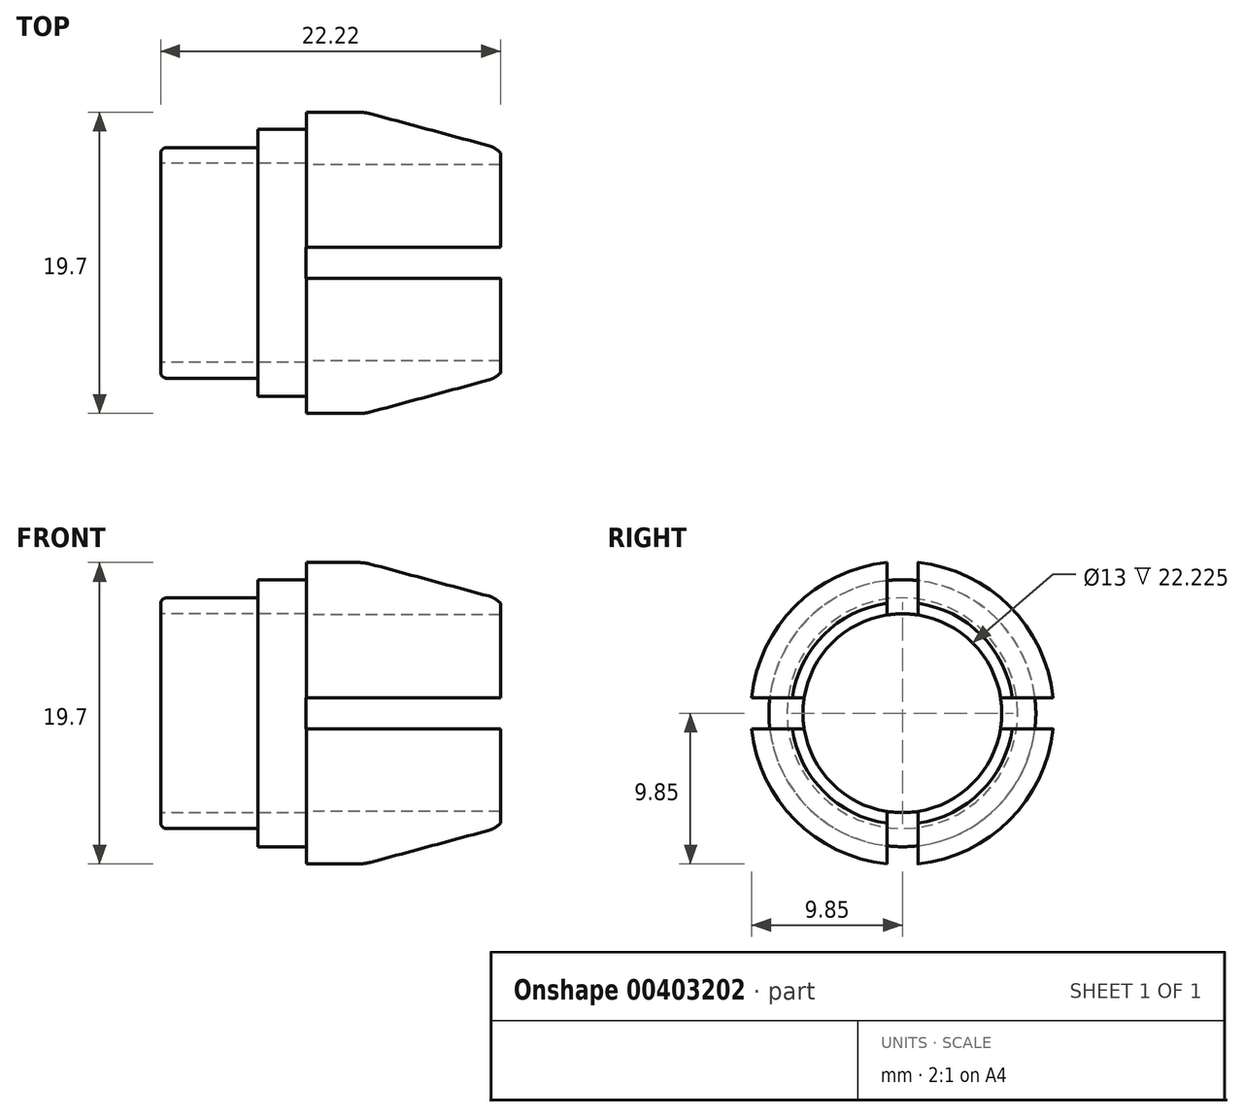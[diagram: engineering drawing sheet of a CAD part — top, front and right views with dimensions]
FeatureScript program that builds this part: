
annotation { "Feature Type Name" : "Feature", "Feature Type Description" : "" }
export const myFeature = defineFeature(function(context is Context, id is Id, definition is map)
    precondition{}
    {
        {
            var Q0;
            Q0=qCreatedBy(makeId("Front.planeOp"),FACE);
            var sketch = newSketch(context, id + "F0", { "sketchPlane" : qUnion([Q0])});
            skLineSegment(sketch, "E0", {"start": v(-22.22, 0) * mm, "end": v(21.75, 0) * mm, "construction": true});
            skLineSegment(sketch, "E1", {"start": v(7.6, 7.73) * mm, "end": v(-0.11, 9.8) * mm});
            skLineSegment(sketch, "E2", {"start": v(-0.93, 9.9) * mm, "end": v(-4.33, 9.9) * mm});
            skArc(sketch, "E3.filletArc", {"start": v(8.37, 7.26) * mm, "mid": v(8.02, 7.55) * mm, "end": v(7.6, 7.73) * mm});
            skLineSegment(sketch, "E4", {"start": v(-4.33, 9.9) * mm, "end": v(-4.33, 8.73) * mm});
            skLineSegment(sketch, "E5", {"start": v(-4.33, 8.73) * mm, "end": v(-7.5, 8.73) * mm});
            skLineSegment(sketch, "E6", {"start": v(-7.5, 8.73) * mm, "end": v(-7.5, 7.54) * mm});
            skLineSegment(sketch, "E7", {"start": v(-7.5, 7.54) * mm, "end": v(-13.45, 7.54) * mm});
            skLineSegment(sketch, "E8", {"start": v(-13.85, 6.5) * mm, "end": v(8.37, 6.5) * mm});
            skLineSegment(sketch, "E9", {"start": v(8.37, 7.26) * mm, "end": v(8.37, 6.5) * mm});
            skLineSegment(sketch, "E10", {"start": v(-13.85, 7.15) * mm, "end": v(-13.85, 6.5) * mm});
            skPoint(sketch, "E11.visualSharp", {"position": v(-13.85, 7.54) * mm});
            skArc(sketch, "E11.filletArc", {"start": v(-13.45, 7.54) * mm, "mid": v(-13.74, 7.43) * mm, "end": v(-13.85, 7.15) * mm});
            skPoint(sketch, "E12.visualSharp", {"position": v(-0.52, 9.9) * mm});
            skArc(sketch, "E12.filletArc", {"start": v(-0.11, 9.8) * mm, "mid": v(-0.52, 9.88) * mm, "end": v(-0.93, 9.9) * mm});
            skSolve(sketch);
        }
        {
            var Q0;
            Q0=makeQuery(id+"F0.imprint","IMPRINT",FACE,{"disambiguationData":[TD([[makeQuery(id+"F0.imprint","IMPRINT",EDGE,{"derivedFrom":sQuery(id+"F0.wireOp",EDGE,"E1")}),1.0]])]});
            var Q1;
            Q1=qSketchRegion(id+"F2",true);
            var Q2;
            Q2=sQuery(id+"F0.wireOp",EDGE,"E0");
            revolve(context, id + "F1", {"entities" : qUnion([Q0, Q1]), "axis" : qUnion([Q2]), "revolveType" : RevolveType.FULL});
        }
        {
            var Q0;
            Q0=qCreatedBy(makeId("Right.planeOp"),FACE);
            var sketch = newSketch(context, id + "F2", { "sketchPlane" : qUnion([Q0])});
            skCircle(sketch, "E13", {"center": v(0, 0) * mm, "radius": 8.53 * mm, "construction": true});
            skPoint(sketch, "E14", {"position": v(0, -8.53) * mm});
            skPoint(sketch, "E15", {"position": v(8.53, 0) * mm});
            skLineSegment(sketch, "E16", {"start": v(1.02, -9.93) * mm, "end": v(-1.02, -9.93) * mm});
            skLineSegment(sketch, "E17", {"start": v(-1.02, -9.93) * mm, "end": v(-1.02, -6.38) * mm});
            skLineSegment(sketch, "E18", {"start": v(-1.02, -6.38) * mm, "end": v(1.02, -6.38) * mm});
            skLineSegment(sketch, "E19", {"start": v(1.02, -6.38) * mm, "end": v(1.02, -9.93) * mm});
            skPoint(sketch, "E20", {"position": v(0, 8.53) * mm});
            skLineSegment(sketch, "E21", {"start": v(1.02, 6.38) * mm, "end": v(-1.02, 6.38) * mm});
            skLineSegment(sketch, "E22", {"start": v(-1.02, 6.38) * mm, "end": v(-1.02, 9.93) * mm});
            skLineSegment(sketch, "E23", {"start": v(-1.02, 9.93) * mm, "end": v(1.02, 9.93) * mm});
            skLineSegment(sketch, "E24", {"start": v(1.02, 9.93) * mm, "end": v(1.02, 6.38) * mm});
            skLineSegment(sketch, "E25", {"start": v(-9.93, -1.02) * mm, "end": v(-9.93, 1.02) * mm});
            skLineSegment(sketch, "E26", {"start": v(-9.93, 1.02) * mm, "end": v(-6.38, 1.02) * mm});
            skLineSegment(sketch, "E27", {"start": v(-6.38, 1.02) * mm, "end": v(-6.38, -1.02) * mm});
            skLineSegment(sketch, "E28", {"start": v(-6.38, -1.02) * mm, "end": v(-9.93, -1.02) * mm});
            skLineSegment(sketch, "E29", {"start": v(-10.98, 0) * mm, "end": v(11.1, 0) * mm, "construction": true});
            skLineSegment(sketch, "E30", {"start": v(6.38, -1.02) * mm, "end": v(6.38, 1.02) * mm});
            skLineSegment(sketch, "E31", {"start": v(6.38, 1.02) * mm, "end": v(9.93, 1.02) * mm});
            skLineSegment(sketch, "E32", {"start": v(9.93, 1.02) * mm, "end": v(9.93, -1.02) * mm});
            skLineSegment(sketch, "E33", {"start": v(9.93, -1.02) * mm, "end": v(6.38, -1.02) * mm});
            skSolve(sketch);
        }
        {
            var Q0;
            Q0=qSketchRegion(id+"F2",true);
            extrude(context, id + "F3", {"entities" : qUnion([Q0]), "operationType" : NewBodyOperationType.REMOVE, "depth" : 25.4 * mm, "hasSecondDirection" : true, "secondDirectionOppositeDirection" : true, "secondDirectionDepth" : 4.34 * mm});
        }
    });
